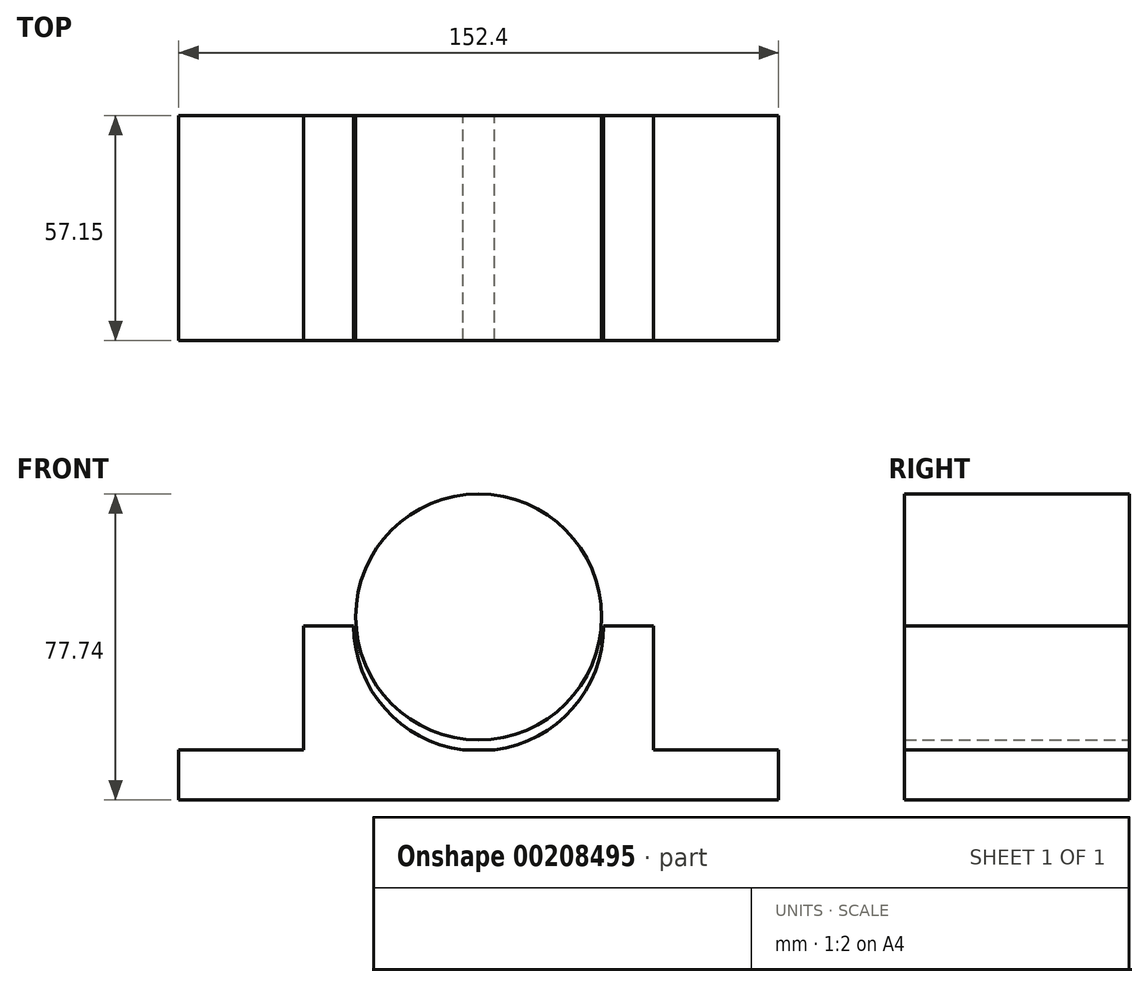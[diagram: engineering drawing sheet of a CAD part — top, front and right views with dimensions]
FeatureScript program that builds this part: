
annotation { "Feature Type Name" : "Feature", "Feature Type Description" : "" }
export const myFeature = defineFeature(function(context is Context, id is Id, definition is map)
    precondition{}
    {
        {
            var Q0;
            Q0=qCreatedBy(makeId("Front.planeOp"),FACE);
            var sketch = newSketch(context, id + "F0", { "sketchPlane" : qUnion([Q0])});
            skLineSegment(sketch, "E0.bottom", {"start": v(-57.8, -40.88) * mm, "end": v(94.6, -40.88) * mm});
            skLineSegment(sketch, "E0.top", {"start": v(-57.8, -53.58) * mm, "end": v(94.6, -53.58) * mm});
            skLineSegment(sketch, "E0.left", {"start": v(-57.8, -40.88) * mm, "end": v(-57.8, -53.58) * mm});
            skLineSegment(sketch, "E0.right", {"start": v(94.6, -40.88) * mm, "end": v(94.6, -53.58) * mm});
            skArc(sketch, "E1", {"start": v(-13.35, -9.39) * mm, "mid": v(-5.43, -30.37) * mm, "end": v(14.38, -40.88) * mm});
            skLineSegment(sketch, "E2.bottom", {"start": v(-13.35, -9.39) * mm, "end": v(-26.05, -9.39) * mm});
            skLineSegment(sketch, "E2.top", {"start": v(-16, -40.88) * mm, "end": v(-26.05, -40.88) * mm});
            skLineSegment(sketch, "E2.right", {"start": v(-26.05, -9.39) * mm, "end": v(-26.05, -40.88) * mm});
            skLineSegment(sketch, "E3.bottom", {"start": v(50.15, -9.39) * mm, "end": v(62.85, -9.39) * mm});
            skLineSegment(sketch, "E3.top", {"start": v(47.5, -40.88) * mm, "end": v(62.85, -40.88) * mm});
            skLineSegment(sketch, "E3.right", {"start": v(62.85, -9.39) * mm, "end": v(62.85, -40.88) * mm});
            skArc(sketch, "E4.trimOffspring", {"start": v(22.42, -40.88) * mm, "mid": v(42.23, -30.37) * mm, "end": v(50.15, -9.39) * mm});
            skCircle(sketch, "E5", {"center": v(18.4, -7.08) * mm, "radius": 31.24 * mm});
            skSolve(sketch);
        }
        {
            var Q0;
            Q0 = qSketchRegion(id + "F0", true);
            extrude(context, id + "F1", {"entities" : qUnion([Q0]), "depth" : 57.15 * mm});
        }
        {
            var Q0;
            Q0 = qSketchRegion(id + "F0", true);
            extrude(context, id + "F2", {"entities" : qUnion([Q0]), "operationType" : NewBodyOperationType.ADD, "depth" : 25.4 * mm});
        }
    });
